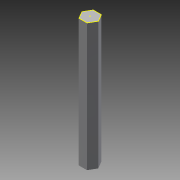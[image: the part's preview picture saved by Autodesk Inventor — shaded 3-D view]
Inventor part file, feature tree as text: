
AUTODESK INVENTOR PART (.ipt)
format: ipt  version: 2014 SP1 (Build 180222100, 222)  size: 78,848 bytes
history: native  units: in
note: dims shown in document units (in); Inventor stores cm internally (conversion verified against a paired STEP export)
features: sketch x2, extrude x1
ambient origin geometry x8: Origin, YZ Plane, XZ Plane, XY Plane, X Axis, Y Axis, Z Axis, Center Point
bodies: Solid1 (feature_tree)
feature tree (3):
  extrude  "Extrusion1"  Depth=4.5in TaperAngle=0.0deg
  sketch  "Sketch2"
  sketch  "Sketch1"  dims[d0=0.5in d1=4.5in d2=0.0in]
